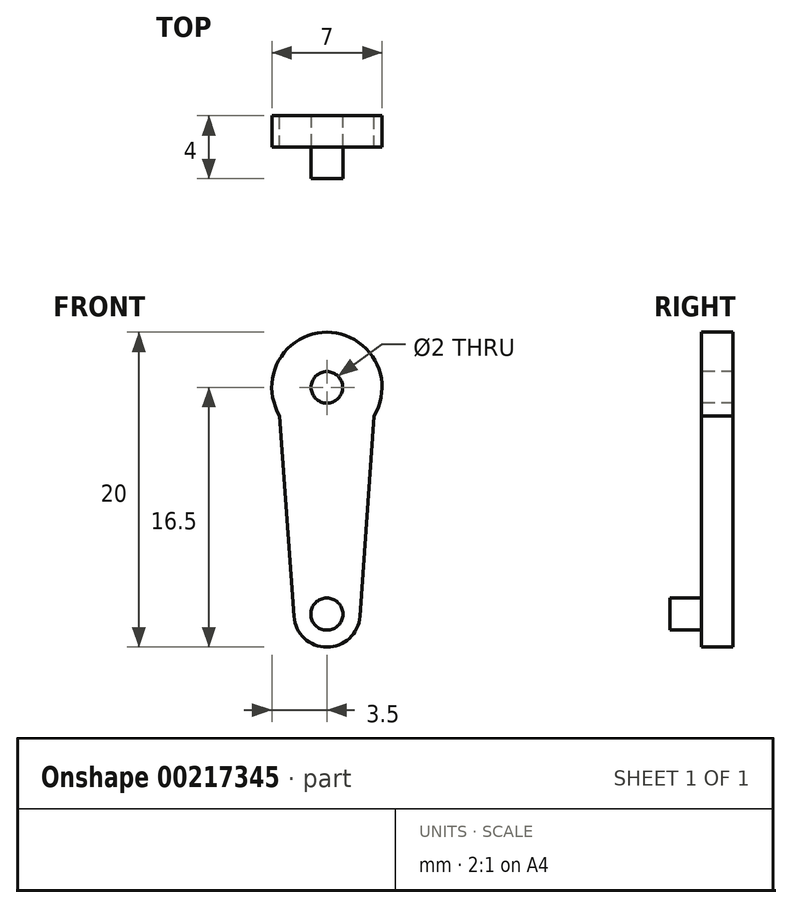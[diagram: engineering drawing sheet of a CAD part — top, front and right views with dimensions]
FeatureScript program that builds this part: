
annotation { "Feature Type Name" : "Feature", "Feature Type Description" : "" }
export const myFeature = defineFeature(function(context is Context, id is Id, definition is map)
    precondition{}
    {
        {
            var Q0;
            Q0=qCreatedBy(makeId("Front.planeOp"),FACE);
            var sketch = newSketch(context, id + "F0", { "sketchPlane" : qUnion([Q0])});
            skArc(sketch, "E0", {"start": v(3, -1.8) * mm, "mid": v(0, 3.5) * mm, "end": v(-3, -1.8) * mm});
            skArc(sketch, "E1", {"start": v(-2.1, -14.55) * mm, "mid": v(0, -16.5) * mm, "end": v(2.1, -14.55) * mm});
            skLineSegment(sketch, "E2", {"start": v(-12.47, 3.5) * mm, "end": v(27.6, 3.5) * mm, "construction": true});
            skLineSegment(sketch, "E3", {"start": v(-17.04, -16.5) * mm, "end": v(23.47, -16.5) * mm, "construction": true});
            skLineSegment(sketch, "E4", {"start": v(-2.1, -14.55) * mm, "end": v(-3, -1.8) * mm});
            skLineSegment(sketch, "E5", {"start": v(2.1, -14.55) * mm, "end": v(3, -1.8) * mm});
            skSolve(sketch);
        }
        {
            var Q0;
            Q0=makeQuery(id+"F0.imprint","IMPRINT",FACE,{"disambiguationData":[TD([[makeQuery(id+"F0.imprint","IMPRINT",EDGE,{"derivedFrom":sQuery(id+"F0.wireOp",EDGE,"E0")}),1.0]])]});
            extrude(context, id + "F1", {"entities" : qUnion([Q0]), "depth" : 2 * mm});
        }
        {
            var Q0;
            Q0=makeQuery(id+"F1.opExtrude","CAP_FACE",FACE,{"disambiguationData":[OSD([sQuery(id+"F0.wireOp",EDGE,"E0"),sQuery(id+"F0.wireOp",EDGE,"E1"),sQuery(id+"F0.wireOp",EDGE,"E4"),sQuery(id+"F0.wireOp",EDGE,"E5")])],"isStart":false});
            var sketch = newSketch(context, id + "F2", { "sketchPlane" : qUnion([Q0])});
            skCircle(sketch, "E6", {"center": v(0, 0) * mm, "radius": 1 * mm});
            skSolve(sketch);
        }
        {
            var Q0;
            Q0=makeQuery(id+"F2.imprint","IMPRINT",FACE,{"disambiguationData":[TD([[makeQuery(id+"F2.imprint","IMPRINT",EDGE,{"derivedFrom":sQuery(id+"F2.wireOp",EDGE,"E6")}),1.0]])]});
            extrude(context, id + "F3", {"entities" : qUnion([Q0]), "operationType" : NewBodyOperationType.REMOVE, "oppositeDirection" : true, "depth" : 25 * mm});
        }
        {
            var Q0;
            Q0=makeQuery(id+"F1.opExtrude","CAP_FACE",FACE,{"disambiguationData":[OSD([sQuery(id+"F0.wireOp",EDGE,"E0"),sQuery(id+"F0.wireOp",EDGE,"E1"),sQuery(id+"F0.wireOp",EDGE,"E4"),sQuery(id+"F0.wireOp",EDGE,"E5")])],"isStart":false});
            var sketch = newSketch(context, id + "F4", { "sketchPlane" : qUnion([Q0])});
            skCircle(sketch, "E7", {"center": v(0, -14.4) * mm, "radius": 1.02 * mm});
            skSolve(sketch);
        }
        {
            var Q0;
            Q0=makeQuery(id+"F4.imprint","IMPRINT",FACE,{"disambiguationData":[TD([[makeQuery(id+"F4.imprint","IMPRINT",EDGE,{"derivedFrom":sQuery(id+"F4.wireOp",EDGE,"E7")}),1.0]])]});
            extrude(context, id + "F5", {"entities" : qUnion([Q0]), "operationType" : NewBodyOperationType.ADD, "depth" : 2 * mm});
        }
    });
